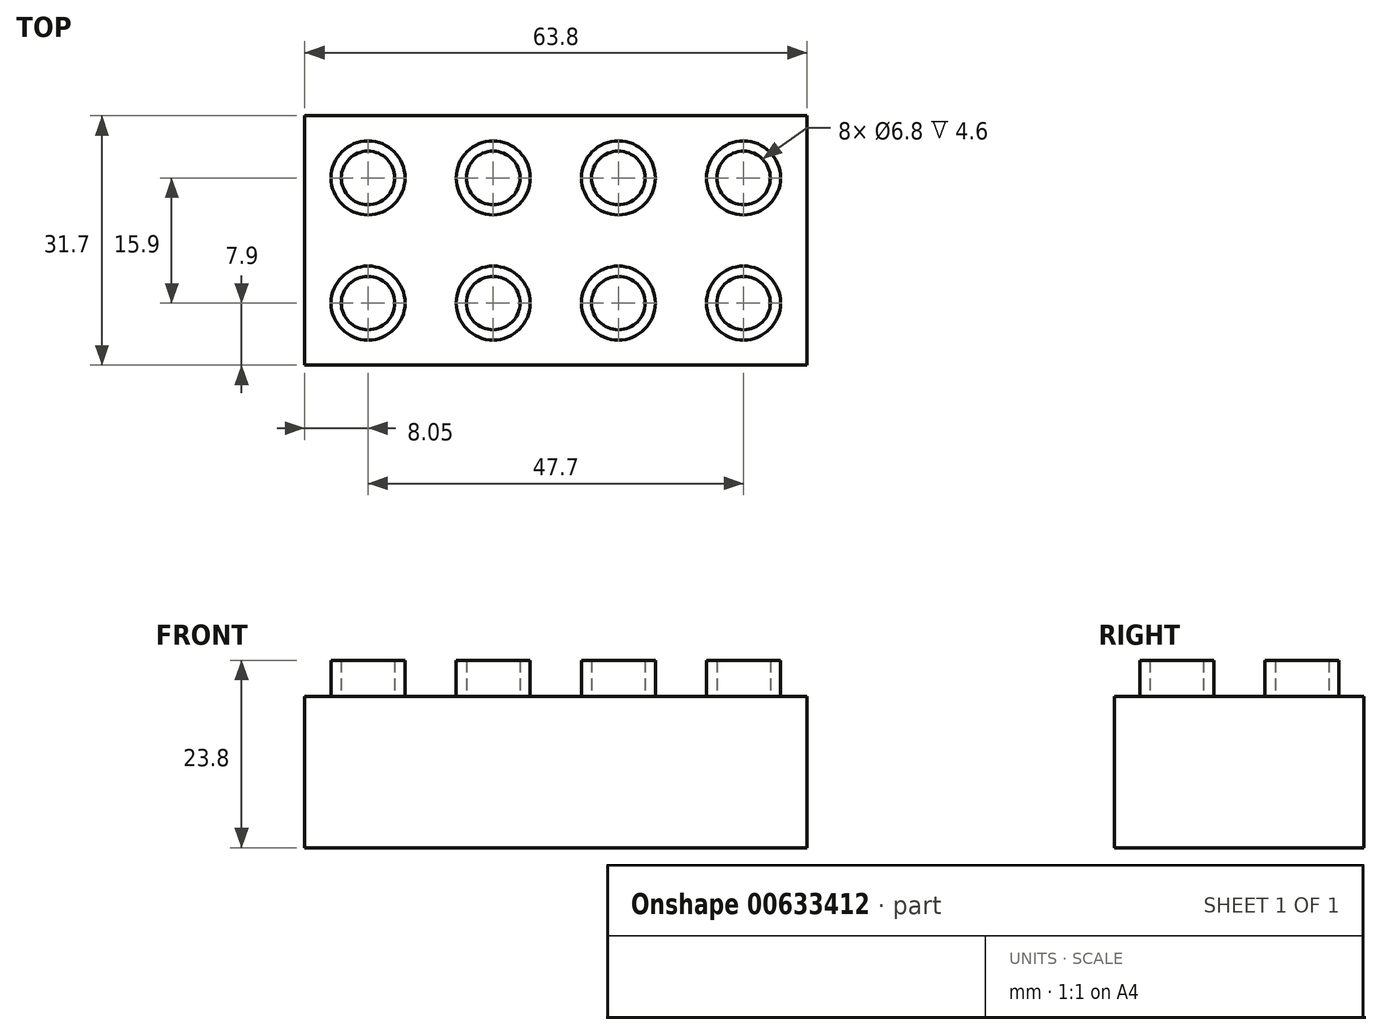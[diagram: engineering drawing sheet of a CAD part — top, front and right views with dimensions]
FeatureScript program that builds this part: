
annotation { "Feature Type Name" : "Feature", "Feature Type Description" : "" }
export const myFeature = defineFeature(function(context is Context, id is Id, definition is map)
    precondition{}
    {
        {
            var Q0;
            Q0=qCreatedBy(makeId("Top.planeOp"),FACE);
            var sketch = newSketch(context, id + "F0", { "sketchPlane" : qUnion([Q0])});
            skLineSegment(sketch, "E0.bottom", {"start": v(-31.9, 15.85) * mm, "end": v(31.9, 15.85) * mm});
            skLineSegment(sketch, "E0.top", {"start": v(-31.9, -15.85) * mm, "end": v(31.9, -15.85) * mm});
            skLineSegment(sketch, "E0.left", {"start": v(-31.9, 15.85) * mm, "end": v(-31.9, -15.85) * mm});
            skLineSegment(sketch, "E0.right", {"start": v(31.9, 15.85) * mm, "end": v(31.9, -15.85) * mm});
            skSolve(sketch);
        }
        {
            var Q0;
            Q0 = qSketchRegion(id + "F0", true);
            extrude(context, id + "F1", {"entities" : qUnion([Q0]), "depth" : 19.2 * mm, "offsetDistance" : 25 * mm});
        }
        {
            var Q0;
            Q0=makeQuery(id+"F1.opExtrude","CAP_FACE",FACE,{"disambiguationData":[OSD([sQuery(id+"F0.wireOp",EDGE,"E0.bottom"),sQuery(id+"F0.wireOp",EDGE,"E0.top"),sQuery(id+"F0.wireOp",EDGE,"E0.left"),sQuery(id+"F0.wireOp",EDGE,"E0.right")])],"isStart":false});
            var sketch = newSketch(context, id + "F2", { "sketchPlane" : qUnion([Q0])});
            skCircle(sketch, "E1", {"center": v(7.95, 7.95) * mm, "radius": 3.4 * mm});
            skCircle(sketch, "E2", {"center": v(7.95, 7.95) * mm, "radius": 4.7 * mm});
            skCircle(sketch, "E3", {"center": v(-7.95, 7.95) * mm, "radius": 3.4 * mm});
            skCircle(sketch, "E4", {"center": v(-7.95, 7.95) * mm, "radius": 4.7 * mm});
            skCircle(sketch, "E5", {"center": v(-23.85, 7.95) * mm, "radius": 3.4 * mm});
            skCircle(sketch, "E6", {"center": v(-23.85, 7.95) * mm, "radius": 4.7 * mm});
            skCircle(sketch, "E7", {"center": v(23.85, 7.95) * mm, "radius": 3.4 * mm});
            skCircle(sketch, "E8", {"center": v(23.85, 7.95) * mm, "radius": 4.7 * mm});
            skCircle(sketch, "E9.MirrorC", {"center": v(23.85, -7.95) * mm, "radius": 3.4 * mm});
            skCircle(sketch, "E10.MirrorC", {"center": v(7.95, -7.95) * mm, "radius": 3.4 * mm});
            skCircle(sketch, "E11.MirrorC", {"center": v(7.95, -7.95) * mm, "radius": 4.7 * mm});
            skCircle(sketch, "E12.MirrorC", {"center": v(-23.85, -7.95) * mm, "radius": 4.7 * mm});
            skCircle(sketch, "E13.MirrorC", {"center": v(-7.95, -7.95) * mm, "radius": 3.4 * mm});
            skCircle(sketch, "E14.MirrorC", {"center": v(23.85, -7.95) * mm, "radius": 4.7 * mm});
            skCircle(sketch, "E15.MirrorC", {"center": v(-23.85, -7.95) * mm, "radius": 3.4 * mm});
            skCircle(sketch, "E16.MirrorC", {"center": v(-7.95, -7.95) * mm, "radius": 4.7 * mm});
            skSolve(sketch);
        }
        {
            var Q0;
            Q0 = qSketchRegion(id + "F2", true);
            extrude(context, id + "F3", {"entities" : qUnion([Q0]), "operationType" : NewBodyOperationType.ADD, "depth" : 4.6 * mm, "offsetDistance" : 25 * mm});
        }
    });
